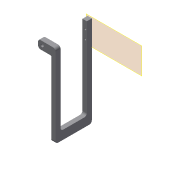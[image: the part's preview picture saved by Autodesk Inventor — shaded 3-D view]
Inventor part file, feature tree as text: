
AUTODESK INVENTOR PART (.ipt)
format: ipt  version: 2019.4 (Build 234330000, 330)  size: 153,600 bytes
history: native  units: mm
features: reference x5, extrude x4, sketch x4, projected_geometry x4, other x4, plane x1, fillet x1
ambient origin geometry x8: Origin, YZ Plane, XZ Plane, XY Plane, X Axis, Y Axis, Z Axis, Center Point
bodies: Solid1 (feature_tree)
feature tree (23):
  plane  "Work Plane1"
  extrude  "Extrusion1"  Depth=145.0mm
  extrude  "Extrusion2"  Depth=14.0mm
  extrude  "Extrusion3"  Depth=118.0mm
  fillet  "Fillet1"  Radius=23.0mm
  extrude  "Extrusion4"  Depth=4.0mm
  sketch  "Sketch1"  dims[d0=5.0mm d1=145.0mm]
  reference  "Reference1"
  reference  "Reference2"
  reference  "Reference3"
  reference  "Reference4"
  sketch  "Sketch2"  dims[d2=8.0mm d3=0.0mm d4=14.0mm]
  projected_geometry  "Projected Loop1"
  sketch  "Sketch3"  dims[d5=50.0mm d6=0.0mm d7=118.0mm d8=23.0mm]
  reference  "Reference5"
  projected_geometry  "Projected Loop2"
  sketch  "Sketch4"  dims[d9=13.0mm d10=5.0mm d11=8.0mm d12=0.0mm d13=4.0mm d14=2.0mm d15=0.0mm]
  projected_geometry  "Projected Loop3"
  projected_geometry  "Projected Loop4"
  other  "Assembly_Opentrons_Imagingunit_v3.iam"
  other  "Assembly_Opentrons_Autofocus_v2:1"
  other  "01_Slide_camera_v1:1"
  other  "00_objectivelens_10x:1"
